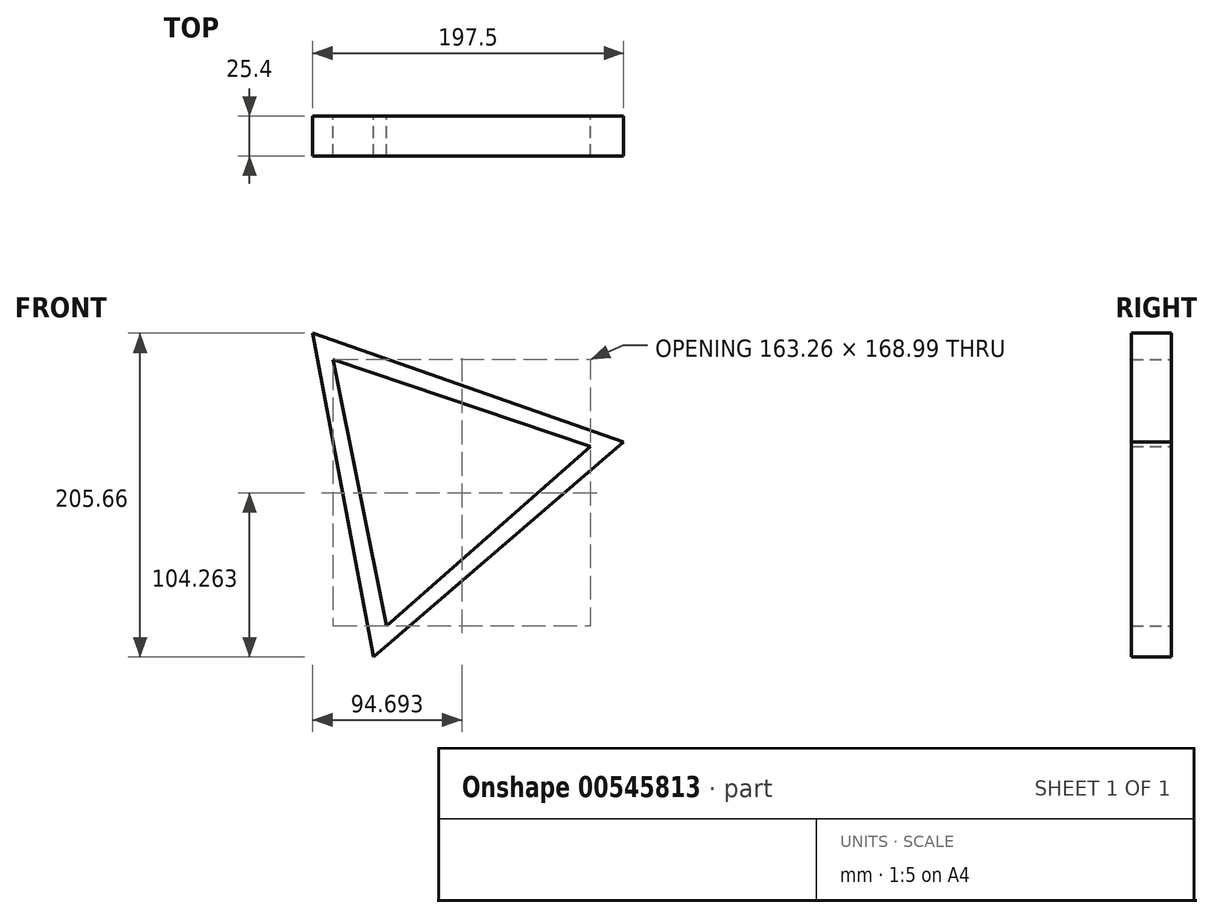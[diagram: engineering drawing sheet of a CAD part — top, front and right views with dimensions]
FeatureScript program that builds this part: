
annotation { "Feature Type Name" : "Feature", "Feature Type Description" : "" }
export const myFeature = defineFeature(function(context is Context, id is Id, definition is map)
    precondition{}
    {
        {
            var Q0;
            Q0=qCreatedBy(makeId("Front.planeOp"),FACE);
            var sketch = newSketch(context, id + "F0", { "sketchPlane" : qUnion([Q0])});
            skCircle(sketch, "E0.cCircle", {"center": v(0, 0) * mm, "radius": 60.41 * mm, "construction": true});
            skLineSegment(sketch, "E0.0", {"start": v(118.74, 22.4) * mm, "end": v(-39.98, -114.03) * mm});
            skLineSegment(sketch, "E0.1", {"start": v(-39.98, -114.03) * mm, "end": v(-78.76, 91.63) * mm});
            skLineSegment(sketch, "E0.2", {"start": v(-78.76, 91.63) * mm, "end": v(118.74, 22.4) * mm});
            skPoint(sketch, "E0.0.midPoint", {"position": v(39.38, -45.82) * mm});
            skCircle(sketch, "E1.cCircle", {"center": v(0, 0) * mm, "radius": 49.75 * mm, "construction": true});
            skLineSegment(sketch, "E1.0", {"start": v(97.56, 19.53) * mm, "end": v(-31.87, -94.26) * mm});
            skLineSegment(sketch, "E1.1", {"start": v(-31.87, -94.26) * mm, "end": v(-65.7, 74.73) * mm});
            skLineSegment(sketch, "E1.2", {"start": v(-65.7, 74.73) * mm, "end": v(97.56, 19.53) * mm});
            skPoint(sketch, "E1.0.midPoint", {"position": v(32.85, -37.36) * mm});
            skSolve(sketch);
        }
        {
            var Q0;
            Q0 = qSketchRegion(id + "F0", true);
            extrude(context, id + "F1", {"entities" : qUnion([Q0]), "depth" : 25.4 * mm, "offsetDistance" : 25.4 * mm});
        }
    });
